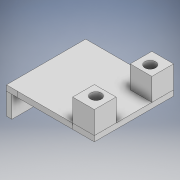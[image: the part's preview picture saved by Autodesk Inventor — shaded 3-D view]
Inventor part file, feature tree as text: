
AUTODESK INVENTOR PART (.ipt)
format: ipt  version: 2020 (Build 240168000, 168)  size: 171,008 bytes
history: native  units: mm
features: sketch x8, extrude x7
ambient origin geometry x8: Origin, YZ Plane, XZ Plane, XY Plane, X Axis, Y Axis, Z Axis, Center Point
bodies: Solid1 (feature_tree)
feature tree (15):
  sketch  "Sketch1"  dims[d4=10.0mm d6=2.0mm]
  sketch  "Sketch2"  dims[d7=2.0mm d8=2.3mm]
  extrude  "Extrusion1"  Depth=2.0mm
  extrude  "Extrusion2"  Depth=2.0mm
  extrude  "Extrusion3"  Depth=7.3mm
  sketch  "Sketch4"  dims[d14=1.7mm d15=1.7mm]
  extrude  "Extrusion4"  Depth=1.7mm
  extrude  "Extrusion5"  Depth=1.0mm TaperAngle=0.0deg
  extrude  "Extrusion6"  Depth=2.0mm
  extrude  "Extrusion7"  Depth=2.0mm
  sketch  "Sketch3"  dims[d9=14.2mm d10=7.3mm]
  sketch  "Sketch5"  dims[d16=4.15mm d17=0.0mm d18=1.0mm d19=0.0mm]
  sketch  "Sketch6"  dims[d20=4.0mm d21=0.0mm d22=2.0mm]
  sketch  "Sketch7"  dims[d23=1.0mm d24=0.0mm d25=2.0mm]
  sketch  "Sketch10"  dims[d26=1.0mm d27=0.0mm d28=2.0mm d29=0.0mm d31=1.0mm d32=4.0mm d33=0.0mm]
